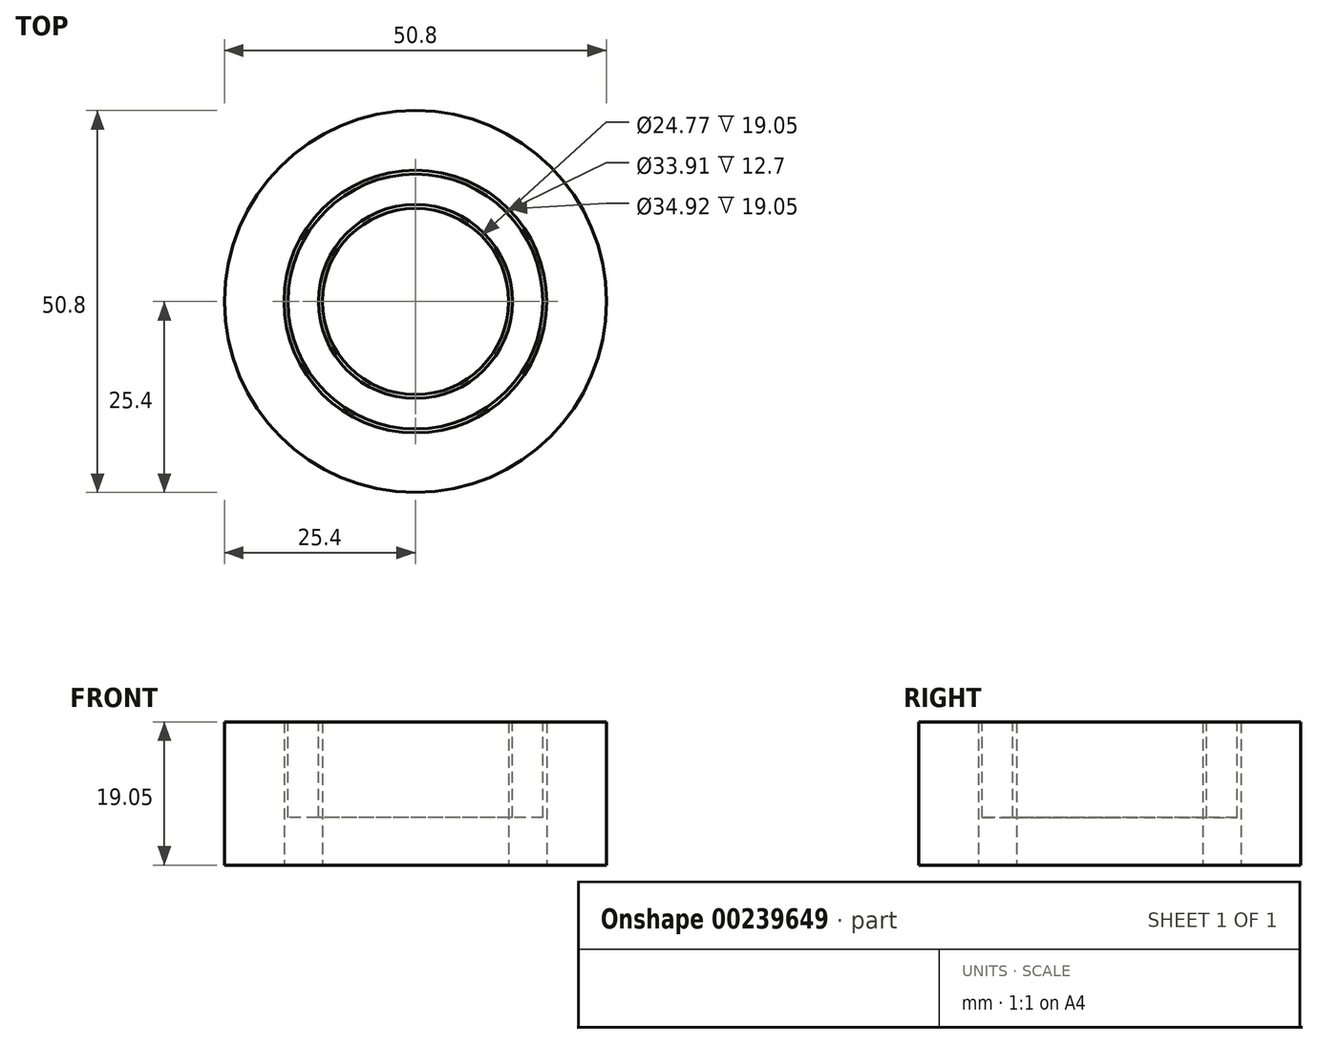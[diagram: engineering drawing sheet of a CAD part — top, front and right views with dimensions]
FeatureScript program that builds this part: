
annotation { "Feature Type Name" : "Feature", "Feature Type Description" : "" }
export const myFeature = defineFeature(function(context is Context, id is Id, definition is map)
    precondition{}
    {
        {
            var Q0;
            Q0=qCreatedBy(makeId("Top.planeOp"),FACE);
            var sketch = newSketch(context, id + "F0", { "sketchPlane" : qUnion([Q0])});
            skCircle(sketch, "E0", {"center": v(0, 0) * mm, "radius": 25.4 * mm});
            skCircle(sketch, "E1", {"center": v(0, 0) * mm, "radius": 17.46 * mm});
            skSolve(sketch);
        }
        {
            var Q0;
            Q0=makeQuery(id+"F0.imprint","IMPRINT",FACE,{"disambiguationData":[TD([[makeQuery(id+"F0.imprint","IMPRINT",EDGE,{"derivedFrom":sQuery(id+"F0.wireOp",EDGE,"E0")}),1.0]])]});
            extrude(context, id + "F1", {"entities" : qUnion([Q0]), "depth" : 19.05 * mm});
        }
        {
            var Q0;
            Q0=qCreatedBy(makeId("Top.planeOp"),FACE);
            var sketch = newSketch(context, id + "F2", { "sketchPlane" : qUnion([Q0])});
            skCircle(sketch, "E2.0", {"center": v(0, 0) * mm, "radius": 17.46 * mm});
            skCircle(sketch, "E3.0", {"center": v(0, 0) * mm, "radius": 12.38 * mm});
            skSolve(sketch);
        }
        {
            var Q0;
            Q0=makeQuery(id+"F2.imprint","IMPRINT",FACE,{"disambiguationData":[TD([[makeQuery(id+"F2.imprint","IMPRINT",EDGE,{"derivedFrom":sQuery(id+"F2.wireOp",EDGE,"E2.0")}),1.0]])]});
            extrude(context, id + "F3", {"entities" : qUnion([Q0]), "depth" : 19.05 * mm});
        }
        {
            var Q0;
            Q0=makeQuery(id+"F3.opExtrude","CAP_FACE",FACE,{"disambiguationData":[OSD([sQuery(id+"F2.wireOp",EDGE,"E2.0"),sQuery(id+"F2.wireOp",EDGE,"E3.0")])],"isStart":false});
            var sketch = newSketch(context, id + "F4", { "sketchPlane" : qUnion([Q0])});
            skCircle(sketch, "E4.0", {"center": v(0, 0) * mm, "radius": 16.95 * mm});
            skCircle(sketch, "E5.0", {"center": v(0, 0) * mm, "radius": 12.9 * mm});
            skSolve(sketch);
        }
        {
            var Q0;
            Q0=makeQuery(id+"F4.imprint","IMPRINT",FACE,{"disambiguationData":[TD([[makeQuery(id+"F4.imprint","IMPRINT",EDGE,{"derivedFrom":sQuery(id+"F4.wireOp",EDGE,"E4.0")}),1.0]])]});
            extrude(context, id + "F5", {"entities" : qUnion([Q0]), "operationType" : NewBodyOperationType.REMOVE, "oppositeDirection" : true, "depth" : 12.7 * mm});
        }
    });
